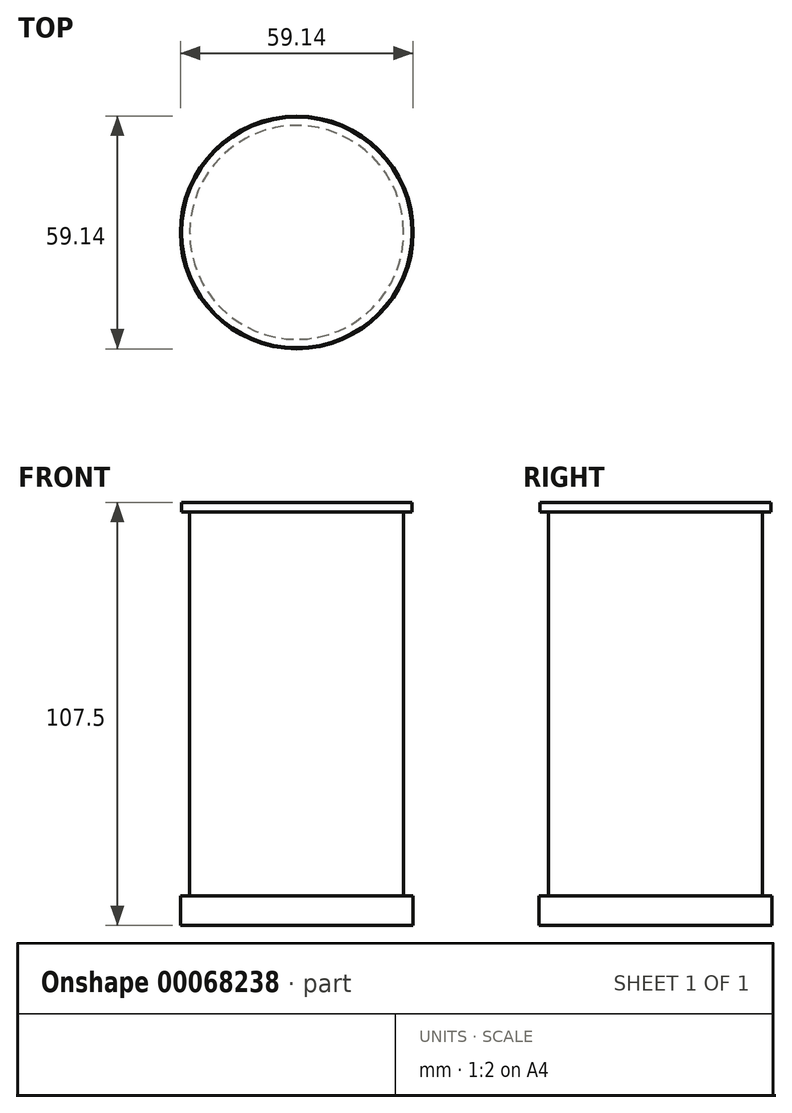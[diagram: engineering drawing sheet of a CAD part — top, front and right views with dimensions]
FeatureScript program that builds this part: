
annotation { "Feature Type Name" : "Feature", "Feature Type Description" : "" }
export const myFeature = defineFeature(function(context is Context, id is Id, definition is map)
    precondition{}
    {
        {
            var Q0;
            Q0=qCreatedBy(makeId("Front.planeOp"),FACE);
            var sketch = newSketch(context, id + "F0", { "sketchPlane" : qUnion([Q0])});
            skLineSegment(sketch, "E0", {"start": v(0, -41.1) * mm, "end": v(29.57, -41.1) * mm});
            skLineSegment(sketch, "E1", {"start": v(29.57, -41.1) * mm, "end": v(29.57, -33.57) * mm});
            skLineSegment(sketch, "E2", {"start": v(29.57, -33.57) * mm, "end": v(27.18, -33.57) * mm});
            skLineSegment(sketch, "E3", {"start": v(27.18, -33.57) * mm, "end": v(27.18, 63.96) * mm});
            skLineSegment(sketch, "E4", {"start": v(27.18, 63.96) * mm, "end": v(29.28, 63.96) * mm});
            skLineSegment(sketch, "E5", {"start": v(29.28, 63.96) * mm, "end": v(29.28, 66.41) * mm});
            skLineSegment(sketch, "E6", {"start": v(29.28, 66.41) * mm, "end": v(0, 66.41) * mm});
            skLineSegment(sketch, "E7", {"start": v(0, 66.41) * mm, "end": v(0, -41.1) * mm});
            skSolve(sketch);
        }
        {
            var Q0;
            Q0=makeQuery(id+"F0.imprint","IMPRINT",FACE,{"disambiguationData":[TD([[makeQuery(id+"F0.imprint","IMPRINT",EDGE,{"derivedFrom":sQuery(id+"F0.wireOp",EDGE,"E0")}),1.0]])]});
            var Q1;
            Q1=sQuery(id+"F0.wireOp",EDGE,"E7");
            revolve(context, id + "F1", {"entities" : qUnion([Q0]), "axis" : qUnion([Q1]), "revolveType" : RevolveType.FULL});
        }
    });
